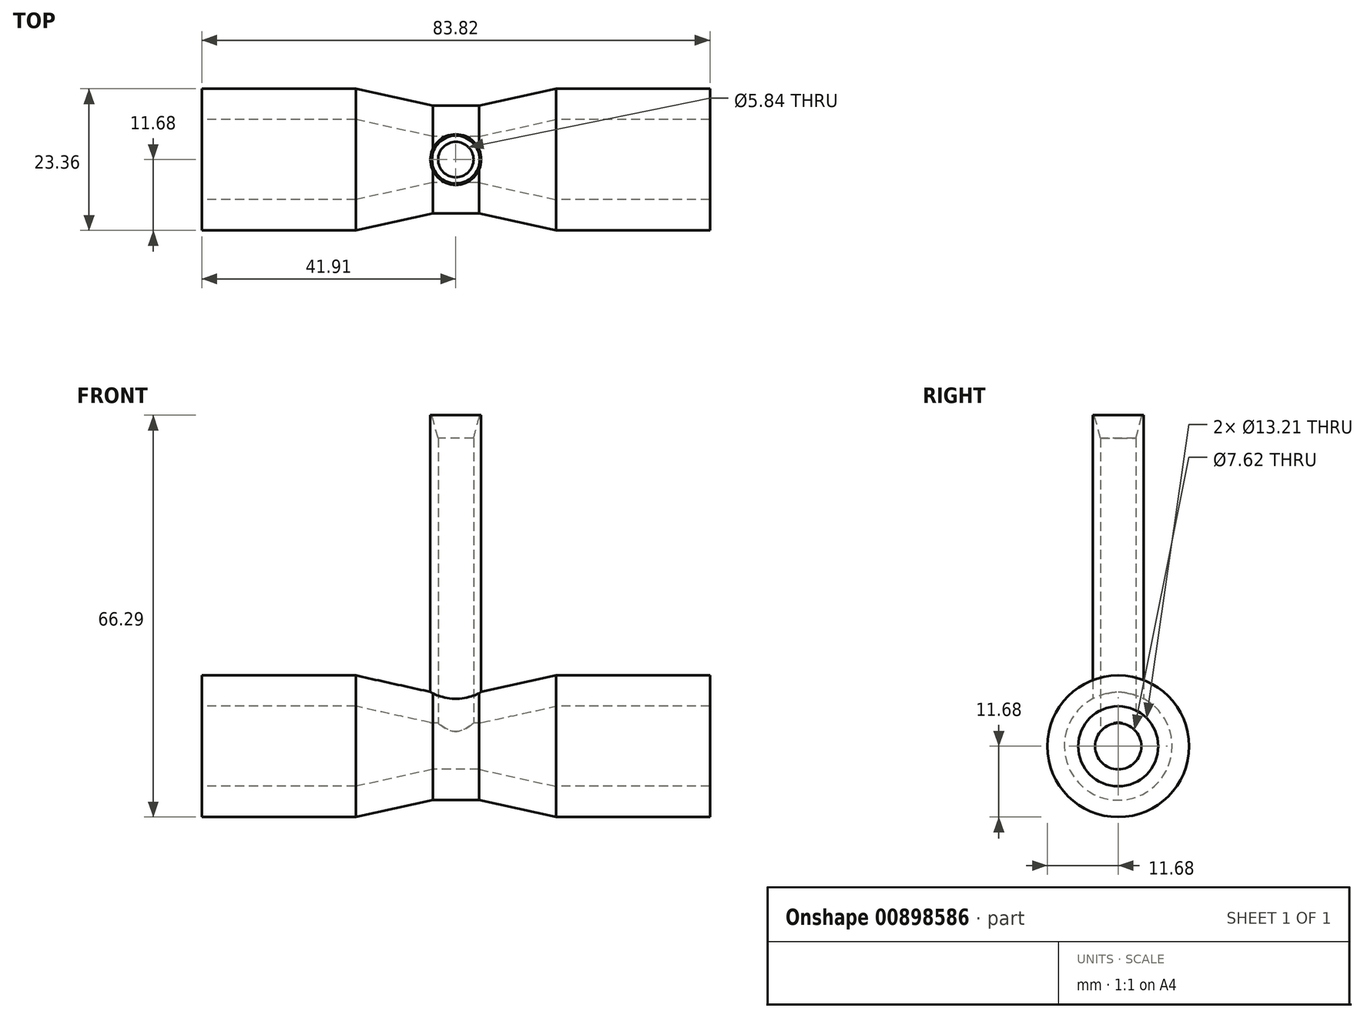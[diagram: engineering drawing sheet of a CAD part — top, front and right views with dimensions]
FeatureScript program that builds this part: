
annotation { "Feature Type Name" : "Feature", "Feature Type Description" : "" }
export const myFeature = defineFeature(function(context is Context, id is Id, definition is map)
    precondition{}
    {
        {
            var Q0;
            Q0=qCreatedBy(makeId("Front.planeOp"),FACE);
            var sketch = newSketch(context, id + "F0", { "sketchPlane" : qUnion([Q0])});
            skLineSegment(sketch, "E0", {"start": v(0, 3.81) * mm, "end": v(-3.8, 3.81) * mm});
            skLineSegment(sketch, "E1", {"start": v(-3.8, 3.8) * mm, "end": v(-16.51, 6.6) * mm});
            skLineSegment(sketch, "E2", {"start": v(-16.51, 6.6) * mm, "end": v(-41.91, 6.6) * mm});
            skLineSegment(sketch, "E3", {"start": v(-41.91, 6.6) * mm, "end": v(-41.91, 11.68) * mm});
            skLineSegment(sketch, "E4", {"start": v(-41.91, 11.68) * mm, "end": v(-16.51, 11.68) * mm});
            skLineSegment(sketch, "E5", {"start": v(-16.51, 11.68) * mm, "end": v(-3.8, 8.9) * mm});
            skLineSegment(sketch, "E6", {"start": v(-3.8, 8.9) * mm, "end": v(0, 8.9) * mm});
            skLineSegment(sketch, "E7.MirrorCS", {"start": v(3.81, 8.9) * mm, "end": v(0, 8.9) * mm});
            skLineSegment(sketch, "E8.MirrorCS", {"start": v(16.51, 11.68) * mm, "end": v(3.81, 8.9) * mm});
            skLineSegment(sketch, "E9.MirrorCS", {"start": v(41.91, 11.68) * mm, "end": v(16.51, 11.68) * mm});
            skLineSegment(sketch, "E10.MirrorCS", {"start": v(41.91, 6.6) * mm, "end": v(41.91, 11.68) * mm});
            skLineSegment(sketch, "E11.MirrorCS", {"start": v(16.51, 6.6) * mm, "end": v(41.91, 6.6) * mm});
            skLineSegment(sketch, "E12.MirrorCS", {"start": v(3.8, 3.8) * mm, "end": v(16.51, 6.6) * mm});
            skLineSegment(sketch, "E13.MirrorCS", {"start": v(0, 3.81) * mm, "end": v(3.8, 3.81) * mm});
            skLineSegment(sketch, "E14", {"start": v(-23.21, 0) * mm, "end": v(29.05, 0) * mm, "construction": true});
            skSolve(sketch);
        }
        {
            var Q0;
            Q0=makeQuery(id+"F0.imprint","IMPRINT",FACE,{"disambiguationData":[TD([[makeQuery(id+"F0.imprint","IMPRINT",EDGE,{"derivedFrom":sQuery(id+"F0.wireOp",EDGE,"E0")}),-1.0]])]});
            var Q1;
            Q1=sQuery(id+"F0.wireOp",EDGE,"E14");
            revolve(context, id + "F1", {"surfaceOperationType" : NewSurfaceOperationType.NEW, "entities" : qUnion([Q0]), "axis" : qUnion([Q1]), "revolveType" : RevolveType.FULL});
        }
        {
            var Q0;
            Q0=qCreatedBy(makeId("Top.planeOp"),FACE);
            cPlane(context, id + "F2", {"entities" : qUnion([Q0]), "cplaneType" : CPlaneType.OFFSET, "offset" : 3.8 * mm, "width" : 152.4 * mm, "height" : 152.4 * mm});
        }
        {
            var Q0;
            Q0=qCreatedBy(id+"F2.planeOp",FACE);
            var sketch = newSketch(context, id + "F3", { "sketchPlane" : qUnion([Q0])});
            skCircle(sketch, "E15", {"center": v(0, 0) * mm, "radius": 2.92 * mm});
            skCircle(sketch, "E16", {"center": v(0, 0) * mm, "radius": 4.2 * mm});
            skSolve(sketch);
        }
        {
            var Q0;
            Q0 = qSketchRegion(id + "F3", true);
            extrude(context, id + "F4", {"entities" : qUnion([Q0]), "operationType" : NewBodyOperationType.ADD, "depth" : 50.8 * mm, "offsetDistance" : 25.4 * mm});
        }
        {
            var Q0;
            Q0=makeQuery(id+"F4.opExtrude","CAP_EDGE",EDGE,{"disambiguationData":[OSD([sQuery(id+"F3.wireOp",EDGE,"E15")])],"isStart":false});
            chamfer(context, id + "F5", {"entities" : qUnion([Q0]), "chamferType" : ChamferType.OFFSET_ANGLE, "width" : 3.8 * mm, "oppositeDirection" : false, "angle" : 15 * degree, "tangentPropagation" : true});
        }
        {
            var Q0;
            Q0=makeQuery(id+"F4.opExtrude","CAP_FACE",FACE,{"disambiguationData":[OSD([sQuery(id+"F3.wireOp",EDGE,"E15"),sQuery(id+"F3.wireOp",EDGE,"E16")])],"isStart":false});
            var sketch = newSketch(context, id + "F6", { "sketchPlane" : qUnion([Q0])});
            skCircle(sketch, "E17", {"center": v(0, 0) * mm, "radius": 2.92 * mm});
            skSolve(sketch);
        }
        {
            var Q0;
            Q0=makeQuery(id+"F6.imprint","IMPRINT",FACE,{"disambiguationData":[TD([[makeQuery(id+"F6.imprint","IMPRINT",EDGE,{"derivedFrom":sQuery(id+"F6.wireOp",EDGE,"E17")}),1.0]])]});
            extrude(context, id + "F7", {"entities" : qUnion([Q0]), "operationType" : NewBodyOperationType.REMOVE, "oppositeDirection" : true, "depth" : 53.34 * mm, "offsetDistance" : 25.4 * mm});
        }
    });
